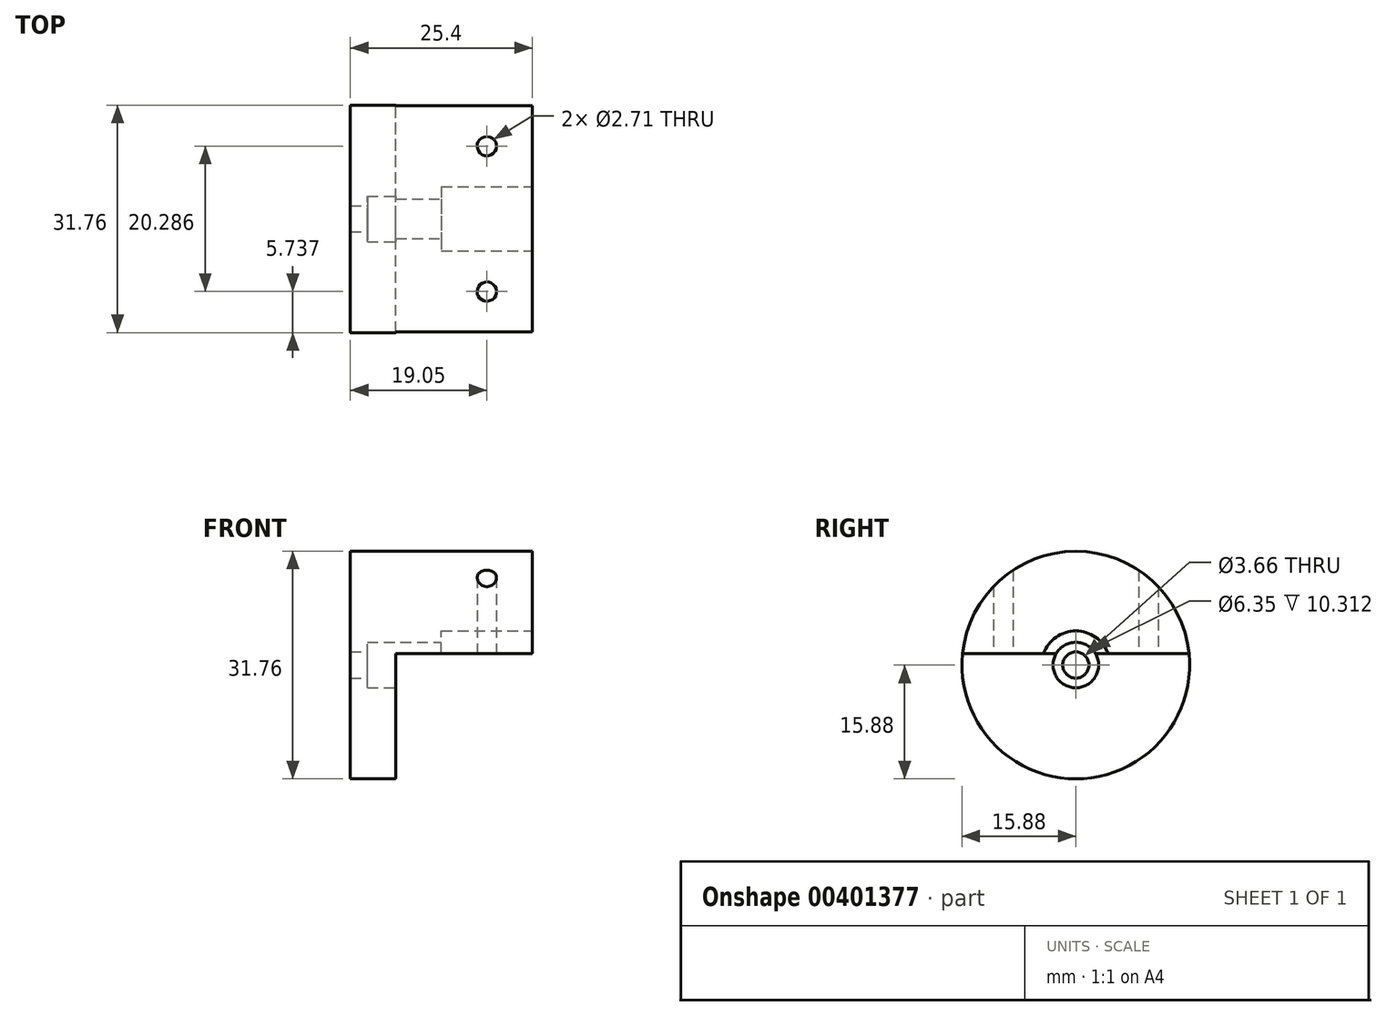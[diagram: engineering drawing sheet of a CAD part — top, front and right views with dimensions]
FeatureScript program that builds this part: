
annotation { "Feature Type Name" : "Feature", "Feature Type Description" : "" }
export const myFeature = defineFeature(function(context is Context, id is Id, definition is map)
    precondition{}
    {
        {
            var Q0;
            Q0=qCreatedBy(makeId("Right.planeOp"),FACE);
            var sketch = newSketch(context, id + "F0", { "sketchPlane" : qUnion([Q0])});
            skCircle(sketch, "E0", {"center": v(0, 0) * mm, "radius": 15.88 * mm});
            skSolve(sketch);
        }
        {
            var Q0;
            Q0 = qSketchRegion(id + "F0", true);
            extrude(context, id + "F1", {"entities" : qUnion([Q0]), "depth" : 25.4 * mm});
        }
        {
            var Q0;
            Q0=makeQuery(id+"F1.opExtrude","CAP_FACE",FACE,{"disambiguationData":[OSD([sQuery(id+"F0.wireOp",EDGE,"E0")])],"isStart":false});
            var sketch = newSketch(context, id + "F2", { "sketchPlane" : qUnion([Q0])});
            skLineSegment(sketch, "E1.bottom", {"start": v(-26.23, 1.59) * mm, "end": v(23.15, 1.59) * mm});
            skLineSegment(sketch, "E1.top", {"start": v(-26.23, -17.45) * mm, "end": v(23.15, -17.45) * mm});
            skLineSegment(sketch, "E1.left", {"start": v(-26.23, 1.59) * mm, "end": v(-26.23, -17.45) * mm});
            skLineSegment(sketch, "E1.right", {"start": v(23.15, 1.59) * mm, "end": v(23.15, -17.45) * mm});
            skSolve(sketch);
        }
        {
            var Q0;
            Q0 = qSketchRegion(id + "F2", true);
            extrude(context, id + "F3", {"entities" : qUnion([Q0]), "operationType" : NewBodyOperationType.REMOVE, "oppositeDirection" : true, "depth" : 19.05 * mm});
        }
        {
            var Q0;
            Q0=makeQuery(id+"F3.boolean.opBoolean","COPY",FACE,{"derivedFrom":makeQuery(id+"F3.opExtrude","CAP_FACE",FACE,{"disambiguationData":[OSD([sQuery(id+"F2.wireOp",EDGE,"cWDqX1qf-G7mn-1U2l-sQfb-lu73WZ1OTyqZ"),sQuery(id+"F2.wireOp",EDGE,"E1.bottom"),sQuery(id+"F2.wireOp",EDGE,"E1.top"),sQuery(id+"F2.wireOp",EDGE,"E1.left"),sQuery(id+"F2.wireOp",EDGE,"E1.right")])],"isStart":false})});
            var sketch = newSketch(context, id + "F4", { "sketchPlane" : qUnion([Q0])});
            skCircle(sketch, "E2", {"center": v(0, 0) * mm, "radius": 1.83 * mm});
            skSolve(sketch);
        }
        {
            var Q0;
            Q0 = qSketchRegion(id + "F4", true);
            extrude(context, id + "F5", {"entities" : qUnion([Q0]), "operationType" : NewBodyOperationType.REMOVE, "endBound" : BoundingType.THROUGH_ALL, "oppositeDirection" : true, "depth" : 25.4 * mm});
        }
        {
            var Q0;
            Q0=makeQuery(id+"F1.opExtrude","CAP_FACE",FACE,{"disambiguationData":[OSD([sQuery(id+"F0.wireOp",EDGE,"E0")])],"isStart":false});
            var sketch = newSketch(context, id + "F6", { "sketchPlane" : qUnion([Q0])});
            skCircle(sketch, "E3", {"center": v(0, 0) * mm, "radius": 4.76 * mm});
            skSolve(sketch);
        }
        {
            var Q0;
            Q0 = qSketchRegion(id + "F6", true);
            extrude(context, id + "F7", {"entities" : qUnion([Q0]), "operationType" : NewBodyOperationType.REMOVE, "oppositeDirection" : true, "depth" : 12.7 * mm});
        }
        {
            var Q0;
            Q0=makeQuery(id+"F1.opExtrude","CAP_FACE",FACE,{"disambiguationData":[OSD([sQuery(id+"F0.wireOp",EDGE,"E0")])],"isStart":false});
            var sketch = newSketch(context, id + "F8", { "sketchPlane" : qUnion([Q0])});
            skCircle(sketch, "E4", {"center": v(0, 0) * mm, "radius": 3.18 * mm});
            skSolve(sketch);
        }
        {
            var Q0;
            Q0 = qSketchRegion(id + "F8", true);
            extrude(context, id + "F9", {"entities" : qUnion([Q0]), "operationType" : NewBodyOperationType.REMOVE, "oppositeDirection" : true, "depth" : 23.01 * mm});
        }
        {
            var Q0;
            {var subQ0=sQuery(id+"F2.wireOp",EDGE,"E1.bottom");Q0=makeQuery(id+"F3.boolean.opBoolean","COPY",FACE,{"derivedFrom":makeQuery(id+"F3.opExtrude","SWEPT_FACE",FACE,{"disambiguationData":[OSD([subQ0]),TDD([makeQuery(id+"F2.imprint","IMPRINT",EDGE,{"disambiguationData":[TD([[makeQuery(id+"F2.imprint","INTERSECT",VERTEX,{"derivedFrom":[subQ0,sQuery(id+"F2.wireOp",EDGE,"E1.left")]}),-1.0]])],"derivedFrom":subQ0}),makeQuery(id+"F2.imprint","IMPRINT",EDGE,{"disambiguationData":[TD([[makeQuery(id+"F2.imprint","INTERSECT",VERTEX,{"disambiguationData":[OD(0.0)],"derivedFrom":[sQuery(id+"F2.wireOp",EDGE,"cWDqX1qf-G7mn-1U2l-sQfb-lu73WZ1OTyqZ"),subQ0]}),1.0]])],"derivedFrom":subQ0})])]})});}
            var sketch = newSketch(context, id + "F10", { "sketchPlane" : qUnion([Q0])});
            skCircle(sketch, "E5", {"center": v(19.05, 10.14) * mm, "radius": 1.35 * mm});
            skLineSegment(sketch, "E6", {"start": v(19.05, 10.14) * mm, "end": v(19.05, 15.8) * mm, "construction": true});
            skLineSegment(sketch, "E7", {"start": v(19.05, 10.14) * mm, "end": v(19.05, 4.5) * mm, "construction": true});
            skCircle(sketch, "E8.MirrorC", {"center": v(19.05, -10.14) * mm, "radius": 1.35 * mm});
            skSolve(sketch);
        }
        {
            var Q0;
            Q0 = qSketchRegion(id + "F10", true);
            extrude(context, id + "F11", {"entities" : qUnion([Q0]), "operationType" : NewBodyOperationType.REMOVE, "endBound" : BoundingType.THROUGH_ALL, "oppositeDirection" : true, "depth" : 25.4 * mm});
        }
    });
